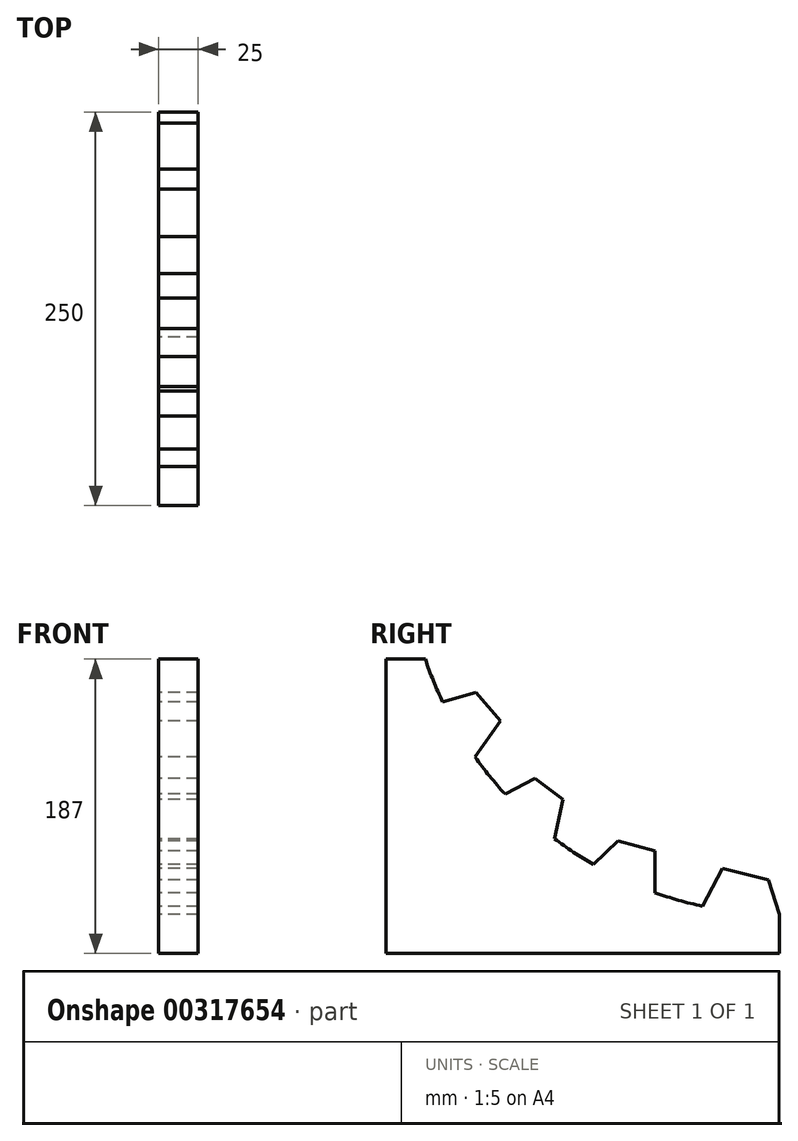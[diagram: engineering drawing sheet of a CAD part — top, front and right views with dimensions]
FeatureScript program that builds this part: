
annotation { "Feature Type Name" : "Feature", "Feature Type Description" : "" }
export const myFeature = defineFeature(function(context is Context, id is Id, definition is map)
    precondition{}
    {
        {
            var Q0;
            Q0=qCreatedBy(makeId("Right.planeOp"),FACE);
            var sketch = newSketch(context, id + "F0", { "sketchPlane" : qUnion([Q0])});
            skLineSegment(sketch, "E0", {"start": v(-36.04, -80.76) * mm, "end": v(-36.04, 106.24) * mm});
            skLineSegment(sketch, "E1", {"start": v(-36.04, -80.76) * mm, "end": v(213.96, -80.76) * mm});
            skLineSegment(sketch, "E2", {"start": v(-36.04, 106.24) * mm, "end": v(-11.04, 106.24) * mm});
            skLineSegment(sketch, "E3", {"start": v(213.96, -80.76) * mm, "end": v(213.96, -55.76) * mm});
            skArc(sketch, "E4", {"start": v(-11.04, 106.24) * mm, "mid": v(-5.94, 92.44) * mm, "end": v(0, 79) * mm});
            skLineSegment(sketch, "E5", {"start": v(213.96, -55.76) * mm, "end": v(206.94, -33.97) * mm});
            skLineSegment(sketch, "E6", {"start": v(206.94, -33.97) * mm, "end": v(177.68, -26.66) * mm});
            skLineSegment(sketch, "E7", {"start": v(177.68, -26.66) * mm, "end": v(165.04, -50.66) * mm});
            skLineSegment(sketch, "E8", {"start": v(0, 79) * mm, "end": v(20.98, 85.2) * mm});
            skLineSegment(sketch, "E9", {"start": v(20.98, 85.2) * mm, "end": v(36.65, 66.92) * mm});
            skLineSegment(sketch, "E10", {"start": v(36.65, 66.92) * mm, "end": v(20.57, 44.07) * mm});
            skLineSegment(sketch, "E11", {"start": v(39.72, 20.49) * mm, "end": v(58.6, 30.34) * mm});
            skLineSegment(sketch, "E12", {"start": v(58.6, 30.34) * mm, "end": v(76.36, 17.28) * mm});
            skLineSegment(sketch, "E13", {"start": v(76.36, 17.28) * mm, "end": v(70.94, -7.8) * mm});
            skLineSegment(sketch, "E14", {"start": v(95.79, -24.23) * mm, "end": v(111.36, -9.36) * mm});
            skLineSegment(sketch, "E15", {"start": v(111.36, -9.36) * mm, "end": v(134.87, -15.63) * mm});
            skLineSegment(sketch, "E16", {"start": v(134.87, -15.63) * mm, "end": v(134.87, -42.18) * mm});
            skArc(sketch, "E17.trimOffspring", {"start": v(20.57, 44.07) * mm, "mid": v(29.77, 31.97) * mm, "end": v(39.72, 20.49) * mm});
            skArc(sketch, "E18.trimOffspring", {"start": v(70.94, -7.8) * mm, "mid": v(83.1, -16.4) * mm, "end": v(95.79, -24.23) * mm});
            skArc(sketch, "E19.trimOffspring", {"start": v(134.87, -42.18) * mm, "mid": v(149.82, -46.92) * mm, "end": v(165.04, -50.66) * mm});
            skSolve(sketch);
        }
        {
            var Q0;
            Q0 = qSketchRegion(id + "F0", true);
            extrude(context, id + "F1", {"entities" : qUnion([Q0]), "depth" : 25 * mm, "offsetDistance" : 25 * mm});
        }
    });
